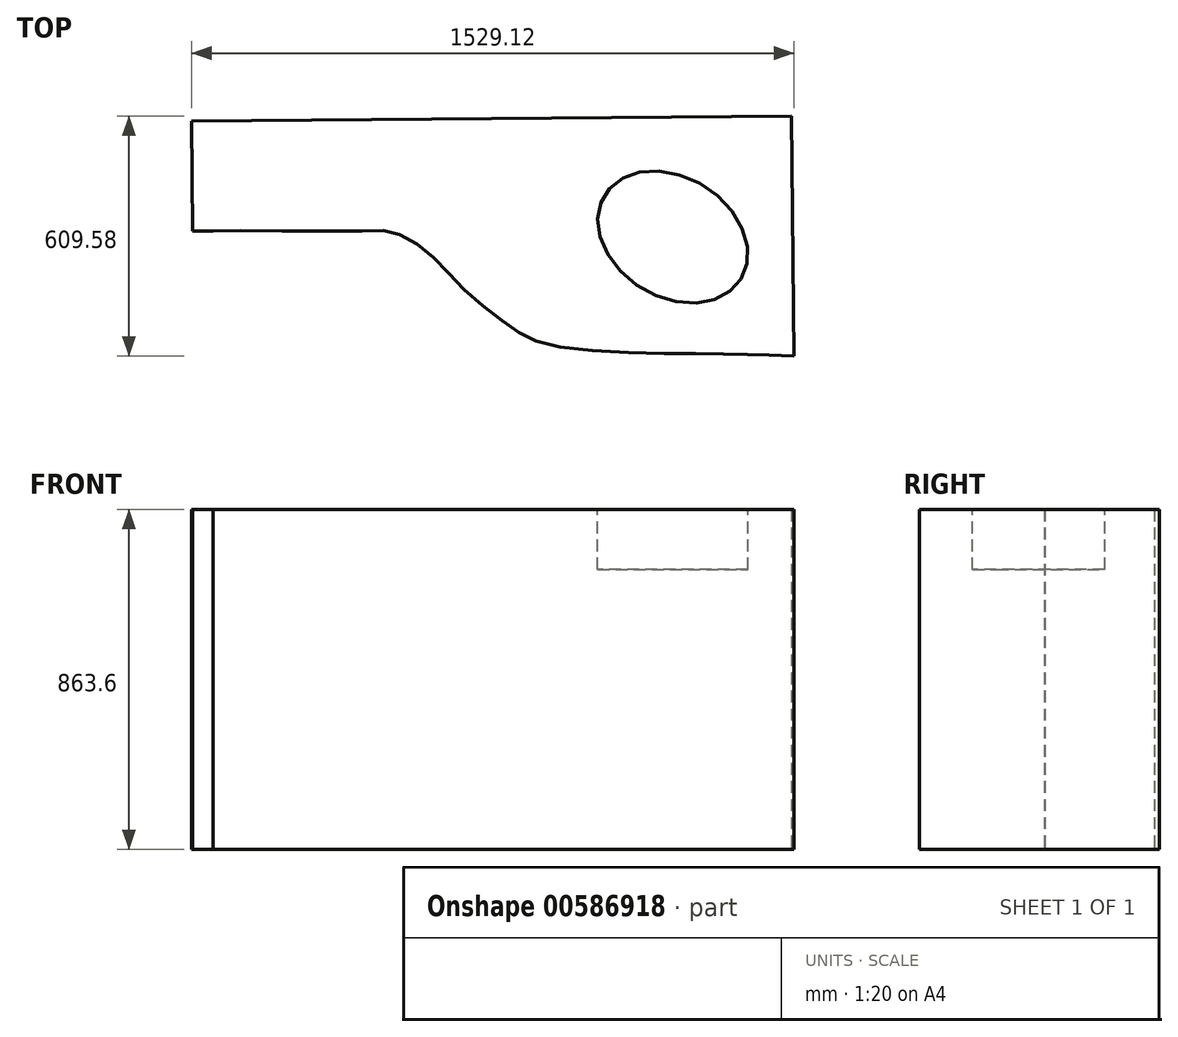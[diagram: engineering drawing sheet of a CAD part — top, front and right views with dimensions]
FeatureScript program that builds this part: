
annotation { "Feature Type Name" : "Feature", "Feature Type Description" : "" }
export const myFeature = defineFeature(function(context is Context, id is Id, definition is map)
    precondition{}
    {
        {
            var Q0;
            Q0=qCreatedBy(makeId("Top.planeOp"),FACE);
            var sketch = newSketch(context, id + "F0", { "sketchPlane" : qUnion([Q0])});
            skLineSegment(sketch, "E0.bottom", {"start": v(0, 0) * mm, "end": v(-1523.95, -12.93) * mm});
            skLineSegment(sketch, "E0.left", {"start": v(0, 0) * mm, "end": v(5.17, -609.58) * mm});
            skLineSegment(sketch, "E0.right", {"start": v(-1523.95, -12.93) * mm, "end": v(-1521.57, -292.32) * mm});
            skLineSegment(sketch, "E1", {"start": v(-1521.57, -292.32) * mm, "end": v(-1470.27, -291.88) * mm});
            skFitSpline(sketch, "E2", {"points": [v(-1470.27, -291.88) * mm, v(-1107.37, -291.88) * mm, v(-1004.63, -297.54) * mm, v(-916.53, -353.16) * mm, v(-831.18, -441.93) * mm, v(-715.1, -534.1) * mm, v(-624.93, -579.57) * mm, v(-342.97, -602.39) * mm, v(-131.03, -605.25) * mm, v(5.17, -609.58) * mm], "startDerivative": vector(960.79, 48.07) * mm, "endDerivative": vector(1613.06, -47.36) * mm});
            skSolve(sketch);
        }
        {
            var Q0;
            Q0=makeQuery(id+"F0.imprint","IMPRINT",FACE,{"disambiguationData":[TD([[makeQuery(id+"F0.imprint","IMPRINT",EDGE,{"derivedFrom":sQuery(id+"F0.wireOp",EDGE,"E0.bottom")}),1.0]])]});
            extrude(context, id + "F1", {"entities" : qUnion([Q0]), "depth" : 863.6 * mm, "offsetDistance" : 25.4 * mm});
        }
        {
            var Q0;
            Q0=makeQuery(id+"F1.opExtrude","CAP_FACE",FACE,{"disambiguationData":[OSD([sQuery(id+"F0.wireOp",EDGE,"E0.bottom"),sQuery(id+"F0.wireOp",EDGE,"E0.left"),sQuery(id+"F0.wireOp",EDGE,"E0.right"),sQuery(id+"F0.wireOp",EDGE,"yOL5Tw4R-CnAu-kNgH-di8C-xmpx5fgGjhbw")])],"isStart":false});
            var sketch = newSketch(context, id + "F2", { "sketchPlane" : qUnion([Q0])});
            skEllipse(sketch, "E3", {"center": v(-302.2, -307.37) * mm, "majorRadius": 203.2 * mm, "minorRadius": 152.4 * mm, "majorAxis": v(0.85, -0.52)});
            skSolve(sketch);
        }
        {
            var Q0;
            Q0=makeQuery(id+"F2.imprint","IMPRINT",FACE,{"disambiguationData":[TD([[makeQuery(id+"F2.imprint","IMPRINT",EDGE,{"derivedFrom":sQuery(id+"F2.wireOp",EDGE,"E3")}),1.0]])]});
            extrude(context, id + "F3", {"entities" : qUnion([Q0]), "operationType" : NewBodyOperationType.REMOVE, "oppositeDirection" : true, "depth" : 152.4 * mm, "offsetDistance" : 25.4 * mm});
        }
    });
